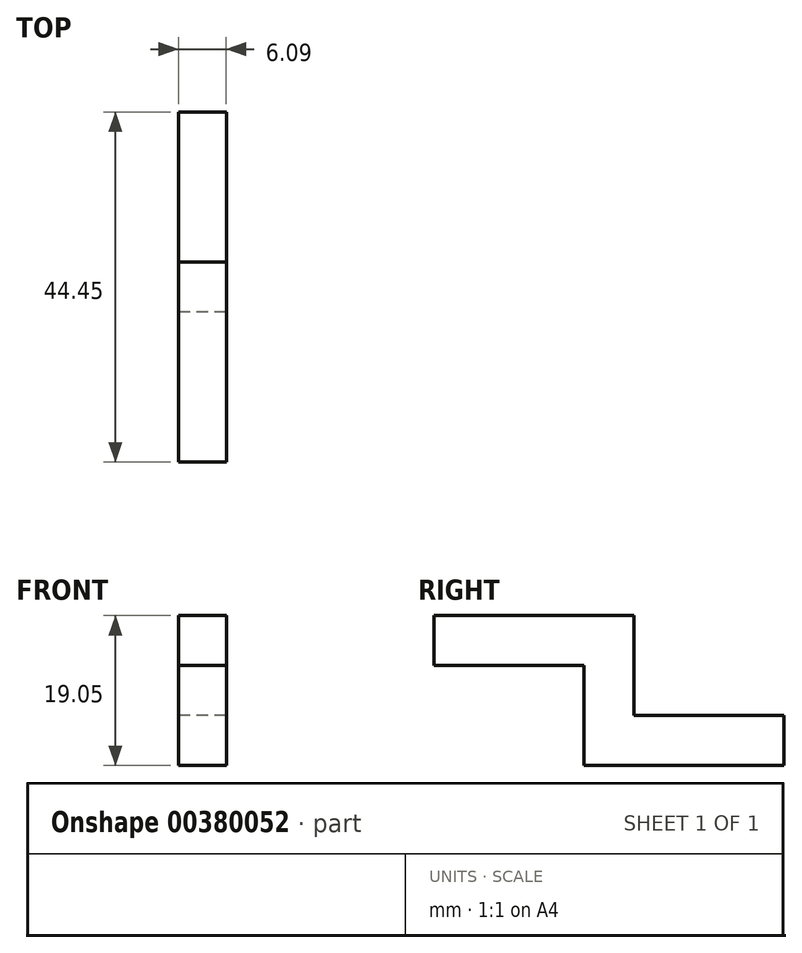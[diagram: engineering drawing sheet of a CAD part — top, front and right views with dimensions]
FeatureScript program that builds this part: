
annotation { "Feature Type Name" : "Feature", "Feature Type Description" : "" }
export const myFeature = defineFeature(function(context is Context, id is Id, definition is map)
    precondition{}
    {
        {
            var Q0;
            Q0=qCreatedBy(makeId("Front.planeOp"),FACE);
            var sketch = newSketch(context, id + "F0", { "sketchPlane" : qUnion([Q0])});
            skLineSegment(sketch, "E0.bottom", {"start": v(-3.32, 19.94) * mm, "end": v(2.77, 19.94) * mm});
            skLineSegment(sketch, "E0.top", {"start": v(-3.32, 13.59) * mm, "end": v(2.77, 13.59) * mm});
            skLineSegment(sketch, "E0.left", {"start": v(-3.32, 19.94) * mm, "end": v(-3.32, 13.59) * mm});
            skLineSegment(sketch, "E0.right", {"start": v(2.77, 19.94) * mm, "end": v(2.77, 13.59) * mm});
            skSolve(sketch);
        }
        {
            var Q0;
            Q0 = qSketchRegion(id + "F0", true);
            extrude(context, id + "F1", {"entities" : qUnion([Q0]), "depth" : 25.4 * mm});
        }
        {
            var Q0;
            Q0=makeQuery(id+"F1.opExtrude","SWEPT_FACE",FACE,{"disambiguationData":[OSD([sQuery(id+"F0.wireOp",EDGE,"E0.top")])]});
            var sketch = newSketch(context, id + "F2", { "sketchPlane" : qUnion([Q0])});
            skLineSegment(sketch, "E1.bottom", {"start": v(2.77, 0) * mm, "end": v(-3.32, 0) * mm});
            skLineSegment(sketch, "E1.top", {"start": v(2.77, 6.35) * mm, "end": v(-3.32, 6.35) * mm});
            skLineSegment(sketch, "E1.left", {"start": v(2.77, 0) * mm, "end": v(2.77, 6.35) * mm});
            skLineSegment(sketch, "E1.right", {"start": v(-3.32, 0) * mm, "end": v(-3.32, 6.35) * mm});
            skSolve(sketch);
        }
        {
            var Q0;
            Q0=makeQuery(id+"F2.imprint","IMPRINT",FACE,{"disambiguationData":[TD([[makeQuery(id+"F2.imprint","IMPRINT",EDGE,{"derivedFrom":sQuery(id+"F2.wireOp",EDGE,"E1.bottom")}),1.0]])]});
            extrude(context, id + "F3", {"entities" : qUnion([Q0]), "operationType" : NewBodyOperationType.ADD, "depth" : 12.7 * mm});
        }
        {
            var Q0;
            Q0=makeQuery(id+"F3.boolean.opBoolean","MERGE",FACE,{"derivedFrom":[makeQuery(id+"F1.opExtrude","CAP_FACE",FACE,{"disambiguationData":[OSD([sQuery(id+"F0.wireOp",EDGE,"E0.bottom"),sQuery(id+"F0.wireOp",EDGE,"E0.top"),sQuery(id+"F0.wireOp",EDGE,"E0.left"),sQuery(id+"F0.wireOp",EDGE,"E0.right")])],"isStart":true}),makeQuery(id+"F3.opExtrude","SWEPT_FACE",FACE,{"disambiguationData":[OSD([sQuery(id+"F2.wireOp",EDGE,"E1.bottom")])]})]});
            var sketch = newSketch(context, id + "F4", { "sketchPlane" : qUnion([Q0])});
            skLineSegment(sketch, "E2.bottom", {"start": v(-2.77, 0.89) * mm, "end": v(3.32, 0.89) * mm});
            skLineSegment(sketch, "E2.top", {"start": v(-2.77, 7.24) * mm, "end": v(3.32, 7.24) * mm});
            skLineSegment(sketch, "E2.left", {"start": v(-2.77, 0.89) * mm, "end": v(-2.77, 7.24) * mm});
            skLineSegment(sketch, "E2.right", {"start": v(3.32, 0.89) * mm, "end": v(3.32, 7.24) * mm});
            skSolve(sketch);
        }
        {
            var Q0;
            Q0=makeQuery(id+"F4.imprint","IMPRINT",FACE,{"disambiguationData":[TD([[makeQuery(id+"F4.imprint","IMPRINT",EDGE,{"derivedFrom":sQuery(id+"F4.wireOp",EDGE,"E2.bottom")}),-1.0]])]});
            extrude(context, id + "F5", {"entities" : qUnion([Q0]), "operationType" : NewBodyOperationType.ADD, "depth" : 19.05 * mm});
        }
    });
